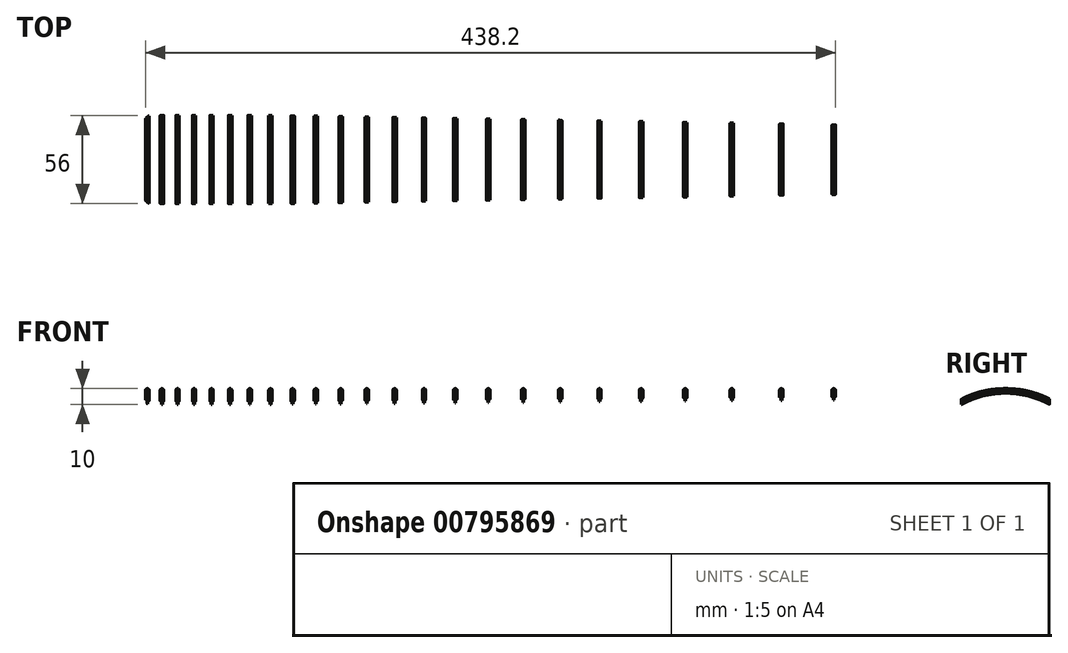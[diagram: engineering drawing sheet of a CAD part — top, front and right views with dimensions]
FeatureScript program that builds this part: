
annotation { "Feature Type Name" : "Feature", "Feature Type Description" : "" }
export const myFeature = defineFeature(function(context is Context, id is Id, definition is map)
    precondition{}
    {
        {
            var Q0;
            Q0=qCreatedBy(makeId("Front.planeOp"),FACE);
            var sketch = newSketch(context, id + "F0", { "sketchPlane" : qUnion([Q0])});
            skLineSegment(sketch, "E0", {"start": v(0.25, 7) * mm, "end": v(471.5, 7) * mm, "construction": true});
            skLineSegment(sketch, "E1", {"start": v(471.5, 7) * mm, "end": v(471.5, 0) * mm, "construction": true});
            skLineSegment(sketch, "E2", {"start": v(436.24, 7) * mm, "end": v(436.24, 0) * mm, "construction": true});
            skLineSegment(sketch, "E3", {"start": v(471.5, 0) * mm, "end": v(0.25, 0) * mm, "construction": true});
            skLineSegment(sketch, "E4", {"start": v(0.25, 0) * mm, "end": v(0.25, 7) * mm, "construction": true});
            skLineSegment(sketch, "E5", {"start": v(402.96, 7) * mm, "end": v(402.96, 0) * mm, "construction": true});
            skLineSegment(sketch, "E6", {"start": v(371.54, 7) * mm, "end": v(371.54, 0) * mm, "construction": true});
            skLineSegment(sketch, "E7", {"start": v(341.88, 7) * mm, "end": v(341.88, 0) * mm, "construction": true});
            skLineSegment(sketch, "E8", {"start": v(313.89, 7) * mm, "end": v(313.89, 0) * mm, "construction": true});
            skLineSegment(sketch, "E9", {"start": v(287.47, 7) * mm, "end": v(287.47, 0) * mm, "construction": true});
            skLineSegment(sketch, "E10", {"start": v(262.53, 7) * mm, "end": v(262.53, 0) * mm, "construction": true});
            skLineSegment(sketch, "E11", {"start": v(239, 7) * mm, "end": v(239, 0) * mm, "construction": true});
            skLineSegment(sketch, "E12", {"start": v(216.79, 7) * mm, "end": v(216.79, 0) * mm, "construction": true});
            skLineSegment(sketch, "E13", {"start": v(195.82, 7) * mm, "end": v(195.82, 0) * mm, "construction": true});
            skLineSegment(sketch, "E14", {"start": v(176.02, 7) * mm, "end": v(176.02, 0) * mm, "construction": true});
            skLineSegment(sketch, "E15", {"start": v(157.34, 7) * mm, "end": v(157.34, 0) * mm, "construction": true});
            skLineSegment(sketch, "E16", {"start": v(139.7, 7) * mm, "end": v(139.7, 0) * mm, "construction": true});
            skLineSegment(sketch, "E17", {"start": v(123.07, 7) * mm, "end": v(123.07, 0) * mm, "construction": true});
            skLineSegment(sketch, "E18", {"start": v(107.36, 7) * mm, "end": v(107.36, 0) * mm, "construction": true});
            skLineSegment(sketch, "E19", {"start": v(92.53, 7) * mm, "end": v(92.53, 0) * mm, "construction": true});
            skLineSegment(sketch, "E20", {"start": v(78.53, 7) * mm, "end": v(78.53, 0) * mm, "construction": true});
            skLineSegment(sketch, "E21", {"start": v(65.32, 7) * mm, "end": v(65.32, 0) * mm, "construction": true});
            skLineSegment(sketch, "E22", {"start": v(52.85, 7) * mm, "end": v(52.85, 0) * mm, "construction": true});
            skLineSegment(sketch, "E23", {"start": v(41.09, 7) * mm, "end": v(41.09, 0) * mm, "construction": true});
            skLineSegment(sketch, "E24", {"start": v(29.98, 7) * mm, "end": v(29.98, 0) * mm, "construction": true});
            skLineSegment(sketch, "E25", {"start": v(19.5, 7) * mm, "end": v(19.5, 0) * mm, "construction": true});
            skLineSegment(sketch, "E26", {"start": v(9.6, 7) * mm, "end": v(9.6, 0) * mm, "construction": true});
            skLineSegment(sketch, "E27", {"start": v(471.76, 7) * mm, "end": v(471.76, 0) * mm});
            skLineSegment(sketch, "E28", {"start": v(471.76, 0) * mm, "end": v(471.26, 0) * mm});
            skLineSegment(sketch, "E29", {"start": v(471.26, 0) * mm, "end": v(471.26, 7) * mm});
            skLineSegment(sketch, "E30", {"start": v(471.26, 7) * mm, "end": v(471.76, 7) * mm});
            skLineSegment(sketch, "E31", {"start": v(436, 7) * mm, "end": v(436.5, 7) * mm});
            skLineSegment(sketch, "E32", {"start": v(436.5, 7) * mm, "end": v(436.5, 0) * mm});
            skLineSegment(sketch, "E33", {"start": v(436.5, 0) * mm, "end": v(436, 0) * mm});
            skLineSegment(sketch, "E34", {"start": v(436, 0) * mm, "end": v(436, 7) * mm});
            skLineSegment(sketch, "E35.bottom", {"start": v(402.7, 7) * mm, "end": v(403.2, 7) * mm});
            skLineSegment(sketch, "E35.top", {"start": v(402.7, 0) * mm, "end": v(403.2, 0) * mm});
            skLineSegment(sketch, "E35.left", {"start": v(402.7, 7) * mm, "end": v(402.7, 0) * mm});
            skLineSegment(sketch, "E35.right", {"start": v(403.2, 7) * mm, "end": v(403.2, 0) * mm});
            skLineSegment(sketch, "E36.bottom", {"start": v(371.29, 7) * mm, "end": v(371.79, 7) * mm});
            skLineSegment(sketch, "E36.top", {"start": v(371.29, 0) * mm, "end": v(371.79, 0) * mm});
            skLineSegment(sketch, "E36.left", {"start": v(371.29, 7) * mm, "end": v(371.29, 0) * mm});
            skLineSegment(sketch, "E36.right", {"start": v(371.79, 7) * mm, "end": v(371.79, 0) * mm});
            skLineSegment(sketch, "E37.bottom", {"start": v(341.63, 7) * mm, "end": v(342.13, 7) * mm});
            skLineSegment(sketch, "E37.top", {"start": v(341.63, 0) * mm, "end": v(342.13, 0) * mm});
            skLineSegment(sketch, "E37.left", {"start": v(341.63, 7) * mm, "end": v(341.63, 0) * mm});
            skLineSegment(sketch, "E37.right", {"start": v(342.13, 7) * mm, "end": v(342.13, 0) * mm});
            skLineSegment(sketch, "E38.bottom", {"start": v(313.64, 7) * mm, "end": v(314.14, 7) * mm});
            skLineSegment(sketch, "E38.top", {"start": v(313.64, 0) * mm, "end": v(314.14, 0) * mm});
            skLineSegment(sketch, "E38.left", {"start": v(313.64, 7) * mm, "end": v(313.64, 0) * mm});
            skLineSegment(sketch, "E38.right", {"start": v(314.14, 7) * mm, "end": v(314.14, 0) * mm});
            skLineSegment(sketch, "E39.bottom", {"start": v(287.22, 7) * mm, "end": v(287.72, 7) * mm});
            skLineSegment(sketch, "E39.top", {"start": v(287.22, 0) * mm, "end": v(287.72, 0) * mm});
            skLineSegment(sketch, "E39.left", {"start": v(287.22, 7) * mm, "end": v(287.22, 0) * mm});
            skLineSegment(sketch, "E39.right", {"start": v(287.72, 7) * mm, "end": v(287.72, 0) * mm});
            skLineSegment(sketch, "E40.bottom", {"start": v(262.28, 7) * mm, "end": v(262.78, 7) * mm});
            skLineSegment(sketch, "E40.top", {"start": v(262.28, 0) * mm, "end": v(262.78, 0) * mm});
            skLineSegment(sketch, "E40.left", {"start": v(262.28, 7) * mm, "end": v(262.28, 0) * mm});
            skLineSegment(sketch, "E40.right", {"start": v(262.78, 7) * mm, "end": v(262.78, 0) * mm});
            skLineSegment(sketch, "E41.bottom", {"start": v(238.75, 7) * mm, "end": v(239.25, 7) * mm});
            skLineSegment(sketch, "E41.top", {"start": v(238.75, 0) * mm, "end": v(239.25, 0) * mm});
            skLineSegment(sketch, "E41.left", {"start": v(238.75, 7) * mm, "end": v(238.75, 0) * mm});
            skLineSegment(sketch, "E41.right", {"start": v(239.25, 7) * mm, "end": v(239.25, 0) * mm});
            skLineSegment(sketch, "E42.bottom", {"start": v(216.54, 7) * mm, "end": v(217.04, 7) * mm});
            skLineSegment(sketch, "E42.top", {"start": v(216.54, 0) * mm, "end": v(217.04, 0) * mm});
            skLineSegment(sketch, "E42.left", {"start": v(216.54, 7) * mm, "end": v(216.54, 0) * mm});
            skLineSegment(sketch, "E42.right", {"start": v(217.04, 7) * mm, "end": v(217.04, 0) * mm});
            skLineSegment(sketch, "E43.bottom", {"start": v(195.57, 7) * mm, "end": v(196.07, 7) * mm});
            skLineSegment(sketch, "E43.top", {"start": v(195.57, 0) * mm, "end": v(196.07, 0) * mm});
            skLineSegment(sketch, "E43.left", {"start": v(195.57, 7) * mm, "end": v(195.57, 0) * mm});
            skLineSegment(sketch, "E43.right", {"start": v(196.07, 7) * mm, "end": v(196.07, 0) * mm});
            skLineSegment(sketch, "E44.bottom", {"start": v(175.77, 7) * mm, "end": v(176.27, 7) * mm});
            skLineSegment(sketch, "E44.top", {"start": v(175.77, 0) * mm, "end": v(176.27, 0) * mm});
            skLineSegment(sketch, "E44.left", {"start": v(175.77, 7) * mm, "end": v(175.77, 0) * mm});
            skLineSegment(sketch, "E44.right", {"start": v(176.27, 7) * mm, "end": v(176.27, 0) * mm});
            skLineSegment(sketch, "E45.bottom", {"start": v(157.1, 7) * mm, "end": v(157.6, 7) * mm});
            skLineSegment(sketch, "E45.top", {"start": v(157.1, 0) * mm, "end": v(157.6, 0) * mm});
            skLineSegment(sketch, "E45.left", {"start": v(157.1, 7) * mm, "end": v(157.1, 0) * mm});
            skLineSegment(sketch, "E45.right", {"start": v(157.6, 7) * mm, "end": v(157.6, 0) * mm});
            skLineSegment(sketch, "E46.bottom", {"start": v(139.46, 7) * mm, "end": v(139.96, 7) * mm});
            skLineSegment(sketch, "E46.top", {"start": v(139.46, 0) * mm, "end": v(139.96, 0) * mm});
            skLineSegment(sketch, "E46.left", {"start": v(139.46, 7) * mm, "end": v(139.46, 0) * mm});
            skLineSegment(sketch, "E46.right", {"start": v(139.96, 7) * mm, "end": v(139.96, 0) * mm});
            skLineSegment(sketch, "E47.bottom", {"start": v(122.82, 7) * mm, "end": v(123.32, 7) * mm});
            skLineSegment(sketch, "E47.top", {"start": v(122.82, 0) * mm, "end": v(123.32, 0) * mm});
            skLineSegment(sketch, "E47.left", {"start": v(122.82, 7) * mm, "end": v(122.82, 0) * mm});
            skLineSegment(sketch, "E47.right", {"start": v(123.32, 7) * mm, "end": v(123.32, 0) * mm});
            skLineSegment(sketch, "E48.bottom", {"start": v(107.1, 7) * mm, "end": v(107.6, 7) * mm});
            skLineSegment(sketch, "E48.top", {"start": v(107.1, 0) * mm, "end": v(107.6, 0) * mm});
            skLineSegment(sketch, "E48.left", {"start": v(107.1, 7) * mm, "end": v(107.1, 0) * mm});
            skLineSegment(sketch, "E48.right", {"start": v(107.6, 7) * mm, "end": v(107.6, 0) * mm});
            skLineSegment(sketch, "E49.bottom", {"start": v(92.28, 7) * mm, "end": v(92.78, 7) * mm});
            skLineSegment(sketch, "E49.top", {"start": v(92.28, 0) * mm, "end": v(92.78, 0) * mm});
            skLineSegment(sketch, "E49.left", {"start": v(92.28, 7) * mm, "end": v(92.28, 0) * mm});
            skLineSegment(sketch, "E49.right", {"start": v(92.78, 7) * mm, "end": v(92.78, 0) * mm});
            skLineSegment(sketch, "E50.bottom", {"start": v(78.28, 7) * mm, "end": v(78.78, 7) * mm});
            skLineSegment(sketch, "E50.top", {"start": v(78.28, 0) * mm, "end": v(78.78, 0) * mm});
            skLineSegment(sketch, "E50.left", {"start": v(78.28, 7) * mm, "end": v(78.28, 0) * mm});
            skLineSegment(sketch, "E50.right", {"start": v(78.78, 7) * mm, "end": v(78.78, 0) * mm});
            skLineSegment(sketch, "E51.bottom", {"start": v(65.07, 7) * mm, "end": v(65.57, 7) * mm});
            skLineSegment(sketch, "E51.top", {"start": v(65.07, 0) * mm, "end": v(65.57, 0) * mm});
            skLineSegment(sketch, "E51.left", {"start": v(65.07, 7) * mm, "end": v(65.07, 0) * mm});
            skLineSegment(sketch, "E51.right", {"start": v(65.57, 7) * mm, "end": v(65.57, 0) * mm});
            skLineSegment(sketch, "E52.bottom", {"start": v(52.6, 7) * mm, "end": v(53.1, 7) * mm});
            skLineSegment(sketch, "E52.top", {"start": v(52.6, 0) * mm, "end": v(53.1, 0) * mm});
            skLineSegment(sketch, "E52.left", {"start": v(52.6, 7) * mm, "end": v(52.6, 0) * mm});
            skLineSegment(sketch, "E52.right", {"start": v(53.1, 7) * mm, "end": v(53.1, 0) * mm});
            skLineSegment(sketch, "E53.bottom", {"start": v(40.84, 7) * mm, "end": v(41.34, 7) * mm});
            skLineSegment(sketch, "E53.top", {"start": v(40.84, 0) * mm, "end": v(41.34, 0) * mm});
            skLineSegment(sketch, "E53.left", {"start": v(40.84, 7) * mm, "end": v(40.84, 0) * mm});
            skLineSegment(sketch, "E53.right", {"start": v(41.34, 7) * mm, "end": v(41.34, 0) * mm});
            skLineSegment(sketch, "E54.bottom", {"start": v(0, 7) * mm, "end": v(0.5, 7) * mm});
            skLineSegment(sketch, "E54.top", {"start": v(0, 0) * mm, "end": v(0.5, 0) * mm});
            skLineSegment(sketch, "E54.left", {"start": v(0, 7) * mm, "end": v(0, 0) * mm});
            skLineSegment(sketch, "E54.right", {"start": v(0.5, 7) * mm, "end": v(0.5, 0) * mm});
            skLineSegment(sketch, "E55.bottom", {"start": v(9.35, 7) * mm, "end": v(9.85, 7) * mm});
            skLineSegment(sketch, "E55.top", {"start": v(9.35, 0) * mm, "end": v(9.85, 0) * mm});
            skLineSegment(sketch, "E55.left", {"start": v(9.35, 7) * mm, "end": v(9.35, 0) * mm});
            skLineSegment(sketch, "E55.right", {"start": v(9.85, 7) * mm, "end": v(9.85, 0) * mm});
            skLineSegment(sketch, "E56.bottom", {"start": v(19.24, 0) * mm, "end": v(19.74, 0) * mm});
            skLineSegment(sketch, "E56.top", {"start": v(19.24, 7) * mm, "end": v(19.74, 7) * mm});
            skLineSegment(sketch, "E56.left", {"start": v(19.24, 0) * mm, "end": v(19.24, 7) * mm});
            skLineSegment(sketch, "E56.right", {"start": v(19.74, 0) * mm, "end": v(19.74, 7) * mm});
            skLineSegment(sketch, "E57.bottom", {"start": v(29.73, 7) * mm, "end": v(30.23, 7) * mm});
            skLineSegment(sketch, "E57.top", {"start": v(29.73, 0) * mm, "end": v(30.23, 0) * mm});
            skLineSegment(sketch, "E57.left", {"start": v(29.73, 7) * mm, "end": v(29.73, 0) * mm});
            skLineSegment(sketch, "E57.right", {"start": v(30.23, 7) * mm, "end": v(30.23, 0) * mm});
            skSolve(sketch);
        }
        {
            var Q0;
            Q0=qCreatedBy(makeId("Front.planeOp"),FACE);
            var sketch = newSketch(context, id + "F1", { "sketchPlane" : qUnion([Q0])});
            skLineSegment(sketch, "E58", {"start": v(436, 5.27) * mm, "end": v(436.5, 5.27) * mm});
            skLineSegment(sketch, "E59", {"start": v(436.5, 5.27) * mm, "end": v(436.5, 6.85) * mm});
            skLineSegment(sketch, "E60", {"start": v(436, 5.27) * mm, "end": v(436, 6.85) * mm});
            skArc(sketch, "E61", {"start": v(435.15, 7.32) * mm, "mid": v(436.24, 8.14) * mm, "end": v(437.34, 7.32) * mm});
            skLineSegment(sketch, "E62", {"start": v(435.39, 7) * mm, "end": v(435.84, 7) * mm});
            skLineSegment(sketch, "E63", {"start": v(437.1, 7) * mm, "end": v(436.64, 7) * mm});
            skPoint(sketch, "E64.visualSharp", {"position": v(437.38, 7) * mm});
            skArc(sketch, "E64.filletArc", {"start": v(437.1, 7) * mm, "mid": v(437.3, 7.1) * mm, "end": v(437.34, 7.32) * mm});
            skPoint(sketch, "E65.visualSharp", {"position": v(435.1, 7) * mm});
            skArc(sketch, "E65.filletArc", {"start": v(435.15, 7.32) * mm, "mid": v(435.19, 7.1) * mm, "end": v(435.39, 7) * mm});
            skPoint(sketch, "E66.visualSharp", {"position": v(436.5, 7) * mm});
            skArc(sketch, "E66.filletArc", {"start": v(436.64, 7) * mm, "mid": v(436.54, 6.96) * mm, "end": v(436.5, 6.85) * mm});
            skPoint(sketch, "E67.visualSharp", {"position": v(436, 7) * mm});
            skArc(sketch, "E67.filletArc", {"start": v(436, 6.85) * mm, "mid": v(435.95, 6.96) * mm, "end": v(435.84, 7) * mm});
            skPoint(sketch, "E68.endSnap0", {"position": v(436.24, 8.14) * mm});
            skLineSegment(sketch, "E69", {"start": v(436.24, 8.14) * mm, "end": v(436.24, -53.3) * mm, "construction": true});
            skLineSegment(sketch, "E70", {"start": v(402.7, 5.27) * mm, "end": v(403.2, 5.27) * mm});
            skLineSegment(sketch, "E71", {"start": v(403.2, 5.27) * mm, "end": v(403.2, 6.85) * mm});
            skLineSegment(sketch, "E72", {"start": v(402.7, 5.27) * mm, "end": v(402.7, 6.85) * mm});
            skArc(sketch, "E73", {"start": v(401.86, 7.32) * mm, "mid": v(402.96, 8.14) * mm, "end": v(404.05, 7.32) * mm});
            skLineSegment(sketch, "E74", {"start": v(402.1, 7) * mm, "end": v(402.56, 7) * mm});
            skLineSegment(sketch, "E75", {"start": v(403.8, 7) * mm, "end": v(403.36, 7) * mm});
            skPoint(sketch, "E76.visualSharp", {"position": v(404.1, 7) * mm});
            skArc(sketch, "E76.filletArc", {"start": v(403.8, 7) * mm, "mid": v(404, 7.1) * mm, "end": v(404.05, 7.32) * mm});
            skPoint(sketch, "E77.visualSharp", {"position": v(401.82, 7) * mm});
            skArc(sketch, "E77.filletArc", {"start": v(401.86, 7.32) * mm, "mid": v(401.9, 7.1) * mm, "end": v(402.1, 7) * mm});
            skPoint(sketch, "E78.visualSharp", {"position": v(403.2, 7) * mm});
            skArc(sketch, "E78.filletArc", {"start": v(403.36, 7) * mm, "mid": v(403.25, 6.96) * mm, "end": v(403.2, 6.85) * mm});
            skPoint(sketch, "E79.visualSharp", {"position": v(402.7, 7) * mm});
            skArc(sketch, "E79.filletArc", {"start": v(402.7, 6.85) * mm, "mid": v(402.66, 6.96) * mm, "end": v(402.56, 7) * mm});
            skPoint(sketch, "E80.endSnap0", {"position": v(402.96, 8.14) * mm});
            skLineSegment(sketch, "E81", {"start": v(402.96, 8.14) * mm, "end": v(402.96, -53.3) * mm, "construction": true});
            skLineSegment(sketch, "E82", {"start": v(371.29, 5.27) * mm, "end": v(371.79, 5.27) * mm});
            skLineSegment(sketch, "E83", {"start": v(371.79, 5.27) * mm, "end": v(371.79, 6.85) * mm});
            skLineSegment(sketch, "E84", {"start": v(371.29, 5.27) * mm, "end": v(371.29, 6.85) * mm});
            skArc(sketch, "E85", {"start": v(370.44, 7.32) * mm, "mid": v(371.54, 8.14) * mm, "end": v(372.63, 7.32) * mm});
            skLineSegment(sketch, "E86", {"start": v(370.68, 7) * mm, "end": v(371.14, 7) * mm});
            skLineSegment(sketch, "E87", {"start": v(372.4, 7) * mm, "end": v(371.94, 7) * mm});
            skPoint(sketch, "E88.visualSharp", {"position": v(372.68, 7) * mm});
            skArc(sketch, "E88.filletArc", {"start": v(372.4, 7) * mm, "mid": v(372.6, 7.1) * mm, "end": v(372.63, 7.32) * mm});
            skPoint(sketch, "E89.visualSharp", {"position": v(370.4, 7) * mm});
            skArc(sketch, "E89.filletArc", {"start": v(370.44, 7.32) * mm, "mid": v(370.48, 7.1) * mm, "end": v(370.68, 7) * mm});
            skPoint(sketch, "E90.visualSharp", {"position": v(371.79, 7) * mm});
            skArc(sketch, "E90.filletArc", {"start": v(371.94, 7) * mm, "mid": v(371.83, 6.96) * mm, "end": v(371.79, 6.85) * mm});
            skPoint(sketch, "E91.visualSharp", {"position": v(371.29, 7) * mm});
            skArc(sketch, "E91.filletArc", {"start": v(371.29, 6.85) * mm, "mid": v(371.24, 6.96) * mm, "end": v(371.14, 7) * mm});
            skPoint(sketch, "E92.endSnap0", {"position": v(371.54, 8.14) * mm});
            skLineSegment(sketch, "E93", {"start": v(371.54, 8.14) * mm, "end": v(371.54, -53.3) * mm, "construction": true});
            skLineSegment(sketch, "E94", {"start": v(341.63, 5.27) * mm, "end": v(342.13, 5.27) * mm});
            skLineSegment(sketch, "E95", {"start": v(342.13, 5.27) * mm, "end": v(342.13, 6.85) * mm});
            skLineSegment(sketch, "E96", {"start": v(341.63, 5.27) * mm, "end": v(341.63, 6.85) * mm});
            skArc(sketch, "E97", {"start": v(340.79, 7.32) * mm, "mid": v(341.88, 8.14) * mm, "end": v(342.97, 7.32) * mm});
            skLineSegment(sketch, "E98", {"start": v(341.03, 7) * mm, "end": v(341.48, 7) * mm});
            skLineSegment(sketch, "E99", {"start": v(342.73, 7) * mm, "end": v(342.28, 7) * mm});
            skPoint(sketch, "E100.visualSharp", {"position": v(343.02, 7) * mm});
            skArc(sketch, "E100.filletArc", {"start": v(342.73, 7) * mm, "mid": v(342.93, 7.1) * mm, "end": v(342.97, 7.32) * mm});
            skPoint(sketch, "E101.visualSharp", {"position": v(340.74, 7) * mm});
            skArc(sketch, "E101.filletArc", {"start": v(340.79, 7.32) * mm, "mid": v(340.83, 7.1) * mm, "end": v(341.03, 7) * mm});
            skPoint(sketch, "E102.visualSharp", {"position": v(342.13, 7) * mm});
            skArc(sketch, "E102.filletArc", {"start": v(342.28, 7) * mm, "mid": v(342.17, 6.96) * mm, "end": v(342.13, 6.85) * mm});
            skPoint(sketch, "E103.visualSharp", {"position": v(341.63, 7) * mm});
            skArc(sketch, "E103.filletArc", {"start": v(341.63, 6.85) * mm, "mid": v(341.59, 6.96) * mm, "end": v(341.48, 7) * mm});
            skPoint(sketch, "E104.endSnap0", {"position": v(341.88, 8.14) * mm});
            skLineSegment(sketch, "E105", {"start": v(341.88, 8.14) * mm, "end": v(341.88, -53.3) * mm, "construction": true});
            skLineSegment(sketch, "E106", {"start": v(313.64, 5.27) * mm, "end": v(314.14, 5.27) * mm});
            skLineSegment(sketch, "E107", {"start": v(314.14, 5.27) * mm, "end": v(314.14, 6.85) * mm});
            skLineSegment(sketch, "E108", {"start": v(313.64, 5.27) * mm, "end": v(313.64, 6.85) * mm});
            skArc(sketch, "E109", {"start": v(312.8, 7.32) * mm, "mid": v(313.89, 8.14) * mm, "end": v(314.98, 7.32) * mm});
            skLineSegment(sketch, "E110", {"start": v(313.03, 7) * mm, "end": v(313.49, 7) * mm});
            skLineSegment(sketch, "E111", {"start": v(314.74, 7) * mm, "end": v(314.29, 7) * mm});
            skPoint(sketch, "E112.visualSharp", {"position": v(315.03, 7) * mm});
            skArc(sketch, "E112.filletArc", {"start": v(314.74, 7) * mm, "mid": v(314.94, 7.1) * mm, "end": v(314.98, 7.32) * mm});
            skPoint(sketch, "E113.visualSharp", {"position": v(312.75, 7) * mm});
            skArc(sketch, "E113.filletArc", {"start": v(312.8, 7.32) * mm, "mid": v(312.83, 7.1) * mm, "end": v(313.03, 7) * mm});
            skPoint(sketch, "E114.visualSharp", {"position": v(314.14, 7) * mm});
            skArc(sketch, "E114.filletArc", {"start": v(314.29, 7) * mm, "mid": v(314.18, 6.96) * mm, "end": v(314.14, 6.85) * mm});
            skPoint(sketch, "E115.visualSharp", {"position": v(313.64, 7) * mm});
            skArc(sketch, "E115.filletArc", {"start": v(313.64, 6.85) * mm, "mid": v(313.6, 6.96) * mm, "end": v(313.49, 7) * mm});
            skPoint(sketch, "E116.endSnap0", {"position": v(313.89, 8.14) * mm});
            skLineSegment(sketch, "E117", {"start": v(313.89, 8.14) * mm, "end": v(313.89, -53.3) * mm, "construction": true});
            skLineSegment(sketch, "E118", {"start": v(287.22, 5.27) * mm, "end": v(287.72, 5.27) * mm});
            skLineSegment(sketch, "E119", {"start": v(287.72, 5.27) * mm, "end": v(287.72, 6.85) * mm});
            skLineSegment(sketch, "E120", {"start": v(287.22, 5.27) * mm, "end": v(287.22, 6.85) * mm});
            skArc(sketch, "E121", {"start": v(286.37, 7.32) * mm, "mid": v(287.47, 8.14) * mm, "end": v(288.56, 7.32) * mm});
            skLineSegment(sketch, "E122", {"start": v(286.61, 7) * mm, "end": v(287.07, 7) * mm});
            skLineSegment(sketch, "E123", {"start": v(288.32, 7) * mm, "end": v(287.87, 7) * mm});
            skPoint(sketch, "E124.visualSharp", {"position": v(288.6, 7) * mm});
            skArc(sketch, "E124.filletArc", {"start": v(288.32, 7) * mm, "mid": v(288.52, 7.1) * mm, "end": v(288.56, 7.32) * mm});
            skPoint(sketch, "E125.visualSharp", {"position": v(286.33, 7) * mm});
            skArc(sketch, "E125.filletArc", {"start": v(286.37, 7.32) * mm, "mid": v(286.41, 7.1) * mm, "end": v(286.61, 7) * mm});
            skPoint(sketch, "E126.visualSharp", {"position": v(287.72, 7) * mm});
            skArc(sketch, "E126.filletArc", {"start": v(287.87, 7) * mm, "mid": v(287.76, 6.96) * mm, "end": v(287.72, 6.85) * mm});
            skPoint(sketch, "E127.visualSharp", {"position": v(287.22, 7) * mm});
            skArc(sketch, "E127.filletArc", {"start": v(287.22, 6.85) * mm, "mid": v(287.17, 6.96) * mm, "end": v(287.07, 7) * mm});
            skPoint(sketch, "E128.endSnap0", {"position": v(287.47, 8.14) * mm});
            skLineSegment(sketch, "E129", {"start": v(287.47, 8.14) * mm, "end": v(287.47, -53.3) * mm, "construction": true});
            skLineSegment(sketch, "E130", {"start": v(262.28, 5.27) * mm, "end": v(262.78, 5.27) * mm});
            skLineSegment(sketch, "E131", {"start": v(262.78, 5.27) * mm, "end": v(262.78, 6.85) * mm});
            skLineSegment(sketch, "E132", {"start": v(262.28, 5.27) * mm, "end": v(262.28, 6.85) * mm});
            skArc(sketch, "E133", {"start": v(261.44, 7.32) * mm, "mid": v(262.53, 8.14) * mm, "end": v(263.63, 7.32) * mm});
            skLineSegment(sketch, "E134", {"start": v(261.68, 7) * mm, "end": v(262.13, 7) * mm});
            skLineSegment(sketch, "E135", {"start": v(263.39, 7) * mm, "end": v(262.93, 7) * mm});
            skPoint(sketch, "E136.visualSharp", {"position": v(263.67, 7) * mm});
            skArc(sketch, "E136.filletArc", {"start": v(263.39, 7) * mm, "mid": v(263.59, 7.1) * mm, "end": v(263.63, 7.32) * mm});
            skPoint(sketch, "E137.visualSharp", {"position": v(261.4, 7) * mm});
            skArc(sketch, "E137.filletArc", {"start": v(261.44, 7.32) * mm, "mid": v(261.48, 7.1) * mm, "end": v(261.68, 7) * mm});
            skPoint(sketch, "E138.visualSharp", {"position": v(262.78, 7) * mm});
            skArc(sketch, "E138.filletArc", {"start": v(262.93, 7) * mm, "mid": v(262.83, 6.96) * mm, "end": v(262.78, 6.85) * mm});
            skPoint(sketch, "E139.visualSharp", {"position": v(262.28, 7) * mm});
            skArc(sketch, "E139.filletArc", {"start": v(262.28, 6.85) * mm, "mid": v(262.24, 6.96) * mm, "end": v(262.13, 7) * mm});
            skPoint(sketch, "E140.endSnap0", {"position": v(262.53, 8.14) * mm});
            skLineSegment(sketch, "E141", {"start": v(262.53, 8.14) * mm, "end": v(262.53, -53.3) * mm, "construction": true});
            skLineSegment(sketch, "E142", {"start": v(238.75, 5.27) * mm, "end": v(239.25, 5.27) * mm});
            skLineSegment(sketch, "E143", {"start": v(239.25, 5.27) * mm, "end": v(239.25, 6.85) * mm});
            skLineSegment(sketch, "E144", {"start": v(238.75, 5.27) * mm, "end": v(238.75, 6.85) * mm});
            skArc(sketch, "E145", {"start": v(237.9, 7.32) * mm, "mid": v(239, 8.14) * mm, "end": v(240.1, 7.32) * mm});
            skLineSegment(sketch, "E146", {"start": v(238.15, 7) * mm, "end": v(238.6, 7) * mm});
            skLineSegment(sketch, "E147", {"start": v(239.86, 7) * mm, "end": v(239.4, 7) * mm});
            skPoint(sketch, "E148.visualSharp", {"position": v(240.14, 7) * mm});
            skArc(sketch, "E148.filletArc", {"start": v(239.86, 7) * mm, "mid": v(240.06, 7.1) * mm, "end": v(240.1, 7.32) * mm});
            skPoint(sketch, "E149.visualSharp", {"position": v(237.86, 7) * mm});
            skArc(sketch, "E149.filletArc", {"start": v(237.9, 7.32) * mm, "mid": v(237.95, 7.1) * mm, "end": v(238.15, 7) * mm});
            skPoint(sketch, "E150.visualSharp", {"position": v(239.25, 7) * mm});
            skArc(sketch, "E150.filletArc", {"start": v(239.4, 7) * mm, "mid": v(239.3, 6.96) * mm, "end": v(239.25, 6.85) * mm});
            skPoint(sketch, "E151.visualSharp", {"position": v(238.75, 7) * mm});
            skArc(sketch, "E151.filletArc", {"start": v(238.75, 6.85) * mm, "mid": v(238.7, 6.96) * mm, "end": v(238.6, 7) * mm});
            skPoint(sketch, "E152.endSnap0", {"position": v(239, 8.14) * mm});
            skLineSegment(sketch, "E153", {"start": v(239, 8.14) * mm, "end": v(239, -53.3) * mm, "construction": true});
            skLineSegment(sketch, "E154", {"start": v(216.54, 5.27) * mm, "end": v(217.04, 5.27) * mm});
            skLineSegment(sketch, "E155", {"start": v(217.04, 5.27) * mm, "end": v(217.04, 6.85) * mm});
            skLineSegment(sketch, "E156", {"start": v(216.54, 5.27) * mm, "end": v(216.54, 6.85) * mm});
            skArc(sketch, "E157", {"start": v(215.7, 7.32) * mm, "mid": v(216.79, 8.14) * mm, "end": v(217.88, 7.32) * mm});
            skLineSegment(sketch, "E158", {"start": v(215.93, 7) * mm, "end": v(216.39, 7) * mm});
            skLineSegment(sketch, "E159", {"start": v(217.64, 7) * mm, "end": v(217.19, 7) * mm});
            skPoint(sketch, "E160.visualSharp", {"position": v(217.93, 7) * mm});
            skArc(sketch, "E160.filletArc", {"start": v(217.64, 7) * mm, "mid": v(217.84, 7.1) * mm, "end": v(217.88, 7.32) * mm});
            skPoint(sketch, "E161.visualSharp", {"position": v(215.65, 7) * mm});
            skArc(sketch, "E161.filletArc", {"start": v(215.7, 7.32) * mm, "mid": v(215.73, 7.1) * mm, "end": v(215.93, 7) * mm});
            skPoint(sketch, "E162.visualSharp", {"position": v(217.04, 7) * mm});
            skArc(sketch, "E162.filletArc", {"start": v(217.19, 7) * mm, "mid": v(217.08, 6.96) * mm, "end": v(217.04, 6.85) * mm});
            skPoint(sketch, "E163.visualSharp", {"position": v(216.54, 7) * mm});
            skArc(sketch, "E163.filletArc", {"start": v(216.54, 6.85) * mm, "mid": v(216.5, 6.96) * mm, "end": v(216.39, 7) * mm});
            skPoint(sketch, "E164.endSnap0", {"position": v(216.79, 8.14) * mm});
            skLineSegment(sketch, "E165", {"start": v(216.79, 8.14) * mm, "end": v(216.79, -53.3) * mm, "construction": true});
            skLineSegment(sketch, "E166", {"start": v(195.57, 5.27) * mm, "end": v(196.07, 5.27) * mm});
            skLineSegment(sketch, "E167", {"start": v(196.07, 5.27) * mm, "end": v(196.07, 6.85) * mm});
            skLineSegment(sketch, "E168", {"start": v(195.57, 5.27) * mm, "end": v(195.57, 6.85) * mm});
            skArc(sketch, "E169", {"start": v(194.72, 7.32) * mm, "mid": v(195.82, 8.14) * mm, "end": v(196.91, 7.32) * mm});
            skLineSegment(sketch, "E170", {"start": v(194.96, 7) * mm, "end": v(195.42, 7) * mm});
            skLineSegment(sketch, "E171", {"start": v(196.67, 7) * mm, "end": v(196.22, 7) * mm});
            skPoint(sketch, "E172.visualSharp", {"position": v(196.96, 7) * mm});
            skArc(sketch, "E172.filletArc", {"start": v(196.67, 7) * mm, "mid": v(196.87, 7.1) * mm, "end": v(196.91, 7.32) * mm});
            skPoint(sketch, "E173.visualSharp", {"position": v(194.68, 7) * mm});
            skArc(sketch, "E173.filletArc", {"start": v(194.72, 7.32) * mm, "mid": v(194.76, 7.1) * mm, "end": v(194.96, 7) * mm});
            skPoint(sketch, "E174.visualSharp", {"position": v(196.07, 7) * mm});
            skArc(sketch, "E174.filletArc", {"start": v(196.22, 7) * mm, "mid": v(196.11, 6.96) * mm, "end": v(196.07, 6.85) * mm});
            skPoint(sketch, "E175.visualSharp", {"position": v(195.57, 7) * mm});
            skArc(sketch, "E175.filletArc", {"start": v(195.57, 6.85) * mm, "mid": v(195.52, 6.96) * mm, "end": v(195.42, 7) * mm});
            skPoint(sketch, "E176.endSnap0", {"position": v(195.82, 8.14) * mm});
            skLineSegment(sketch, "E177", {"start": v(195.82, 8.14) * mm, "end": v(195.82, -53.3) * mm, "construction": true});
            skLineSegment(sketch, "E178", {"start": v(175.77, 5.27) * mm, "end": v(176.27, 5.27) * mm});
            skLineSegment(sketch, "E179", {"start": v(176.27, 5.27) * mm, "end": v(176.27, 6.85) * mm});
            skLineSegment(sketch, "E180", {"start": v(175.77, 5.27) * mm, "end": v(175.77, 6.85) * mm});
            skArc(sketch, "E181", {"start": v(174.93, 7.32) * mm, "mid": v(176.02, 8.14) * mm, "end": v(177.12, 7.32) * mm});
            skLineSegment(sketch, "E182", {"start": v(175.17, 7) * mm, "end": v(175.62, 7) * mm});
            skLineSegment(sketch, "E183", {"start": v(176.88, 7) * mm, "end": v(176.42, 7) * mm});
            skPoint(sketch, "E184.visualSharp", {"position": v(177.16, 7) * mm});
            skArc(sketch, "E184.filletArc", {"start": v(176.88, 7) * mm, "mid": v(177.08, 7.1) * mm, "end": v(177.12, 7.32) * mm});
            skPoint(sketch, "E185.visualSharp", {"position": v(174.88, 7) * mm});
            skArc(sketch, "E185.filletArc", {"start": v(174.93, 7.32) * mm, "mid": v(174.97, 7.1) * mm, "end": v(175.17, 7) * mm});
            skPoint(sketch, "E186.visualSharp", {"position": v(176.27, 7) * mm});
            skArc(sketch, "E186.filletArc", {"start": v(176.42, 7) * mm, "mid": v(176.32, 6.96) * mm, "end": v(176.27, 6.85) * mm});
            skPoint(sketch, "E187.visualSharp", {"position": v(175.77, 7) * mm});
            skArc(sketch, "E187.filletArc", {"start": v(175.77, 6.85) * mm, "mid": v(175.73, 6.96) * mm, "end": v(175.62, 7) * mm});
            skPoint(sketch, "E188.endSnap0", {"position": v(176.02, 8.14) * mm});
            skLineSegment(sketch, "E189", {"start": v(176.02, 8.14) * mm, "end": v(176.02, -53.3) * mm, "construction": true});
            skLineSegment(sketch, "E190", {"start": v(157.1, 5.27) * mm, "end": v(157.6, 5.27) * mm});
            skLineSegment(sketch, "E191", {"start": v(157.6, 5.27) * mm, "end": v(157.6, 6.85) * mm});
            skLineSegment(sketch, "E192", {"start": v(157.1, 5.27) * mm, "end": v(157.1, 6.85) * mm});
            skArc(sketch, "E193", {"start": v(156.25, 7.32) * mm, "mid": v(157.34, 8.14) * mm, "end": v(158.44, 7.32) * mm});
            skLineSegment(sketch, "E194", {"start": v(156.49, 7) * mm, "end": v(156.94, 7) * mm});
            skLineSegment(sketch, "E195", {"start": v(158.2, 7) * mm, "end": v(157.74, 7) * mm});
            skPoint(sketch, "E196.visualSharp", {"position": v(158.48, 7) * mm});
            skArc(sketch, "E196.filletArc", {"start": v(158.2, 7) * mm, "mid": v(158.4, 7.1) * mm, "end": v(158.44, 7.32) * mm});
            skPoint(sketch, "E197.visualSharp", {"position": v(156.2, 7) * mm});
            skArc(sketch, "E197.filletArc", {"start": v(156.25, 7.32) * mm, "mid": v(156.29, 7.1) * mm, "end": v(156.49, 7) * mm});
            skPoint(sketch, "E198.visualSharp", {"position": v(157.6, 7) * mm});
            skArc(sketch, "E198.filletArc", {"start": v(157.74, 7) * mm, "mid": v(157.64, 6.96) * mm, "end": v(157.6, 6.85) * mm});
            skPoint(sketch, "E199.visualSharp", {"position": v(157.1, 7) * mm});
            skArc(sketch, "E199.filletArc", {"start": v(157.1, 6.85) * mm, "mid": v(157.05, 6.96) * mm, "end": v(156.94, 7) * mm});
            skPoint(sketch, "E200.endSnap0", {"position": v(157.34, 8.14) * mm});
            skLineSegment(sketch, "E201", {"start": v(157.34, 8.14) * mm, "end": v(157.34, -53.3) * mm, "construction": true});
            skLineSegment(sketch, "E202", {"start": v(139.46, 5.27) * mm, "end": v(139.96, 5.27) * mm});
            skLineSegment(sketch, "E203", {"start": v(139.96, 5.27) * mm, "end": v(139.96, 6.85) * mm});
            skLineSegment(sketch, "E204", {"start": v(139.46, 5.27) * mm, "end": v(139.46, 6.85) * mm});
            skArc(sketch, "E205", {"start": v(138.62, 7.32) * mm, "mid": v(139.7, 8.14) * mm, "end": v(140.8, 7.32) * mm});
            skLineSegment(sketch, "E206", {"start": v(138.86, 7) * mm, "end": v(139.3, 7) * mm});
            skLineSegment(sketch, "E207", {"start": v(140.56, 7) * mm, "end": v(140.1, 7) * mm});
            skPoint(sketch, "E208.visualSharp", {"position": v(140.85, 7) * mm});
            skArc(sketch, "E208.filletArc", {"start": v(140.56, 7) * mm, "mid": v(140.76, 7.1) * mm, "end": v(140.8, 7.32) * mm});
            skPoint(sketch, "E209.visualSharp", {"position": v(138.57, 7) * mm});
            skArc(sketch, "E209.filletArc", {"start": v(138.62, 7.32) * mm, "mid": v(138.66, 7.1) * mm, "end": v(138.86, 7) * mm});
            skPoint(sketch, "E210.visualSharp", {"position": v(139.96, 7) * mm});
            skArc(sketch, "E210.filletArc", {"start": v(140.1, 7) * mm, "mid": v(140, 6.96) * mm, "end": v(139.96, 6.85) * mm});
            skPoint(sketch, "E211.visualSharp", {"position": v(139.46, 7) * mm});
            skArc(sketch, "E211.filletArc", {"start": v(139.46, 6.85) * mm, "mid": v(139.42, 6.96) * mm, "end": v(139.3, 7) * mm});
            skPoint(sketch, "E212.endSnap0", {"position": v(139.7, 8.14) * mm});
            skLineSegment(sketch, "E213", {"start": v(139.7, 8.14) * mm, "end": v(139.7, -53.3) * mm, "construction": true});
            skLineSegment(sketch, "E214", {"start": v(122.82, 5.27) * mm, "end": v(123.32, 5.27) * mm});
            skLineSegment(sketch, "E215", {"start": v(123.32, 5.27) * mm, "end": v(123.32, 6.85) * mm});
            skLineSegment(sketch, "E216", {"start": v(122.82, 5.27) * mm, "end": v(122.82, 6.85) * mm});
            skArc(sketch, "E217", {"start": v(121.97, 7.32) * mm, "mid": v(123.07, 8.14) * mm, "end": v(124.16, 7.32) * mm});
            skLineSegment(sketch, "E218", {"start": v(122.21, 7) * mm, "end": v(122.67, 7) * mm});
            skLineSegment(sketch, "E219", {"start": v(123.92, 7) * mm, "end": v(123.47, 7) * mm});
            skPoint(sketch, "E220.visualSharp", {"position": v(124.2, 7) * mm});
            skArc(sketch, "E220.filletArc", {"start": v(123.92, 7) * mm, "mid": v(124.12, 7.1) * mm, "end": v(124.16, 7.32) * mm});
            skPoint(sketch, "E221.visualSharp", {"position": v(121.93, 7) * mm});
            skArc(sketch, "E221.filletArc", {"start": v(121.97, 7.32) * mm, "mid": v(122.01, 7.1) * mm, "end": v(122.21, 7) * mm});
            skPoint(sketch, "E222.visualSharp", {"position": v(123.32, 7) * mm});
            skArc(sketch, "E222.filletArc", {"start": v(123.47, 7) * mm, "mid": v(123.36, 6.96) * mm, "end": v(123.32, 6.85) * mm});
            skPoint(sketch, "E223.visualSharp", {"position": v(122.82, 7) * mm});
            skArc(sketch, "E223.filletArc", {"start": v(122.82, 6.85) * mm, "mid": v(122.77, 6.96) * mm, "end": v(122.67, 7) * mm});
            skPoint(sketch, "E224.endSnap0", {"position": v(123.07, 8.14) * mm});
            skLineSegment(sketch, "E225", {"start": v(123.07, 8.14) * mm, "end": v(123.07, -53.3) * mm, "construction": true});
            skLineSegment(sketch, "E226", {"start": v(107.1, 5.27) * mm, "end": v(107.6, 5.27) * mm});
            skLineSegment(sketch, "E227", {"start": v(107.6, 5.27) * mm, "end": v(107.6, 6.85) * mm});
            skLineSegment(sketch, "E228", {"start": v(107.1, 5.27) * mm, "end": v(107.1, 6.85) * mm});
            skArc(sketch, "E229", {"start": v(106.26, 7.32) * mm, "mid": v(107.36, 8.14) * mm, "end": v(108.45, 7.32) * mm});
            skLineSegment(sketch, "E230", {"start": v(106.5, 7) * mm, "end": v(106.96, 7) * mm});
            skLineSegment(sketch, "E231", {"start": v(108.21, 7) * mm, "end": v(107.76, 7) * mm});
            skPoint(sketch, "E232.visualSharp", {"position": v(108.5, 7) * mm});
            skArc(sketch, "E232.filletArc", {"start": v(108.21, 7) * mm, "mid": v(108.41, 7.1) * mm, "end": v(108.45, 7.32) * mm});
            skPoint(sketch, "E233.visualSharp", {"position": v(106.22, 7) * mm});
            skArc(sketch, "E233.filletArc", {"start": v(106.26, 7.32) * mm, "mid": v(106.3, 7.1) * mm, "end": v(106.5, 7) * mm});
            skPoint(sketch, "E234.visualSharp", {"position": v(107.6, 7) * mm});
            skArc(sketch, "E234.filletArc", {"start": v(107.76, 7) * mm, "mid": v(107.65, 6.96) * mm, "end": v(107.6, 6.85) * mm});
            skPoint(sketch, "E235.visualSharp", {"position": v(107.1, 7) * mm});
            skArc(sketch, "E235.filletArc", {"start": v(107.1, 6.85) * mm, "mid": v(107.06, 6.96) * mm, "end": v(106.96, 7) * mm});
            skPoint(sketch, "E236.endSnap0", {"position": v(107.36, 8.14) * mm});
            skLineSegment(sketch, "E237", {"start": v(107.36, 8.14) * mm, "end": v(107.36, -53.3) * mm, "construction": true});
            skLineSegment(sketch, "E238", {"start": v(92.28, 5.27) * mm, "end": v(92.78, 5.27) * mm});
            skLineSegment(sketch, "E239", {"start": v(92.78, 5.27) * mm, "end": v(92.78, 6.85) * mm});
            skLineSegment(sketch, "E240", {"start": v(92.28, 5.27) * mm, "end": v(92.28, 6.85) * mm});
            skArc(sketch, "E241", {"start": v(91.43, 7.32) * mm, "mid": v(92.53, 8.14) * mm, "end": v(93.62, 7.32) * mm});
            skLineSegment(sketch, "E242", {"start": v(91.67, 7) * mm, "end": v(92.13, 7) * mm});
            skLineSegment(sketch, "E243", {"start": v(93.38, 7) * mm, "end": v(92.93, 7) * mm});
            skPoint(sketch, "E244.visualSharp", {"position": v(93.67, 7) * mm});
            skArc(sketch, "E244.filletArc", {"start": v(93.38, 7) * mm, "mid": v(93.58, 7.1) * mm, "end": v(93.62, 7.32) * mm});
            skPoint(sketch, "E245.visualSharp", {"position": v(91.39, 7) * mm});
            skArc(sketch, "E245.filletArc", {"start": v(91.43, 7.32) * mm, "mid": v(91.47, 7.1) * mm, "end": v(91.67, 7) * mm});
            skPoint(sketch, "E246.visualSharp", {"position": v(92.78, 7) * mm});
            skArc(sketch, "E246.filletArc", {"start": v(92.93, 7) * mm, "mid": v(92.82, 6.96) * mm, "end": v(92.78, 6.85) * mm});
            skPoint(sketch, "E247.visualSharp", {"position": v(92.28, 7) * mm});
            skArc(sketch, "E247.filletArc", {"start": v(92.28, 6.85) * mm, "mid": v(92.23, 6.96) * mm, "end": v(92.13, 7) * mm});
            skPoint(sketch, "E248.endSnap0", {"position": v(92.53, 8.14) * mm});
            skLineSegment(sketch, "E249", {"start": v(92.53, 8.14) * mm, "end": v(92.53, -53.3) * mm, "construction": true});
            skLineSegment(sketch, "E250", {"start": v(78.28, 5.27) * mm, "end": v(78.78, 5.27) * mm});
            skLineSegment(sketch, "E251", {"start": v(78.78, 5.27) * mm, "end": v(78.78, 6.85) * mm});
            skLineSegment(sketch, "E252", {"start": v(78.28, 5.27) * mm, "end": v(78.28, 6.85) * mm});
            skArc(sketch, "E253", {"start": v(77.44, 7.32) * mm, "mid": v(78.53, 8.14) * mm, "end": v(79.63, 7.32) * mm});
            skLineSegment(sketch, "E254", {"start": v(77.68, 7) * mm, "end": v(78.13, 7) * mm});
            skLineSegment(sketch, "E255", {"start": v(79.39, 7) * mm, "end": v(78.93, 7) * mm});
            skPoint(sketch, "E256.visualSharp", {"position": v(79.67, 7) * mm});
            skArc(sketch, "E256.filletArc", {"start": v(79.39, 7) * mm, "mid": v(79.59, 7.1) * mm, "end": v(79.63, 7.32) * mm});
            skPoint(sketch, "E257.visualSharp", {"position": v(77.4, 7) * mm});
            skArc(sketch, "E257.filletArc", {"start": v(77.44, 7.32) * mm, "mid": v(77.48, 7.1) * mm, "end": v(77.68, 7) * mm});
            skPoint(sketch, "E258.visualSharp", {"position": v(78.78, 7) * mm});
            skArc(sketch, "E258.filletArc", {"start": v(78.93, 7) * mm, "mid": v(78.83, 6.96) * mm, "end": v(78.78, 6.85) * mm});
            skPoint(sketch, "E259.visualSharp", {"position": v(78.28, 7) * mm});
            skArc(sketch, "E259.filletArc", {"start": v(78.28, 6.85) * mm, "mid": v(78.24, 6.96) * mm, "end": v(78.13, 7) * mm});
            skPoint(sketch, "E260.endSnap0", {"position": v(78.53, 8.14) * mm});
            skLineSegment(sketch, "E261", {"start": v(78.53, 8.14) * mm, "end": v(78.53, -53.3) * mm, "construction": true});
            skLineSegment(sketch, "E262", {"start": v(65.07, 5.27) * mm, "end": v(65.57, 5.27) * mm});
            skLineSegment(sketch, "E263", {"start": v(65.57, 5.27) * mm, "end": v(65.57, 6.85) * mm});
            skLineSegment(sketch, "E264", {"start": v(65.07, 5.27) * mm, "end": v(65.07, 6.85) * mm});
            skArc(sketch, "E265", {"start": v(64.23, 7.32) * mm, "mid": v(65.32, 8.14) * mm, "end": v(66.42, 7.32) * mm});
            skLineSegment(sketch, "E266", {"start": v(64.47, 7) * mm, "end": v(64.92, 7) * mm});
            skLineSegment(sketch, "E267", {"start": v(66.18, 7) * mm, "end": v(65.72, 7) * mm});
            skPoint(sketch, "E268.visualSharp", {"position": v(66.46, 7) * mm});
            skArc(sketch, "E268.filletArc", {"start": v(66.18, 7) * mm, "mid": v(66.38, 7.1) * mm, "end": v(66.42, 7.32) * mm});
            skPoint(sketch, "E269.visualSharp", {"position": v(64.18, 7) * mm});
            skArc(sketch, "E269.filletArc", {"start": v(64.23, 7.32) * mm, "mid": v(64.27, 7.1) * mm, "end": v(64.47, 7) * mm});
            skPoint(sketch, "E270.visualSharp", {"position": v(65.57, 7) * mm});
            skArc(sketch, "E270.filletArc", {"start": v(65.72, 7) * mm, "mid": v(65.62, 6.96) * mm, "end": v(65.57, 6.85) * mm});
            skPoint(sketch, "E271.visualSharp", {"position": v(65.07, 7) * mm});
            skArc(sketch, "E271.filletArc", {"start": v(65.07, 6.85) * mm, "mid": v(65.03, 6.96) * mm, "end": v(64.92, 7) * mm});
            skPoint(sketch, "E272.endSnap0", {"position": v(65.32, 8.14) * mm});
            skLineSegment(sketch, "E273", {"start": v(65.32, 8.14) * mm, "end": v(65.32, -53.3) * mm, "construction": true});
            skLineSegment(sketch, "E274", {"start": v(52.6, 5.27) * mm, "end": v(53.1, 5.27) * mm});
            skLineSegment(sketch, "E275", {"start": v(53.1, 5.27) * mm, "end": v(53.1, 6.85) * mm});
            skLineSegment(sketch, "E276", {"start": v(52.6, 5.27) * mm, "end": v(52.6, 6.85) * mm});
            skArc(sketch, "E277", {"start": v(51.76, 7.32) * mm, "mid": v(52.85, 8.14) * mm, "end": v(53.95, 7.32) * mm});
            skLineSegment(sketch, "E278", {"start": v(52, 7) * mm, "end": v(52.45, 7) * mm});
            skLineSegment(sketch, "E279", {"start": v(53.7, 7) * mm, "end": v(53.25, 7) * mm});
            skPoint(sketch, "E280.visualSharp", {"position": v(54, 7) * mm});
            skArc(sketch, "E280.filletArc", {"start": v(53.7, 7) * mm, "mid": v(53.9, 7.1) * mm, "end": v(53.95, 7.32) * mm});
            skPoint(sketch, "E281.visualSharp", {"position": v(51.71, 7) * mm});
            skArc(sketch, "E281.filletArc", {"start": v(51.76, 7.32) * mm, "mid": v(51.8, 7.1) * mm, "end": v(52, 7) * mm});
            skPoint(sketch, "E282.visualSharp", {"position": v(53.1, 7) * mm});
            skArc(sketch, "E282.filletArc", {"start": v(53.25, 7) * mm, "mid": v(53.15, 6.96) * mm, "end": v(53.1, 6.85) * mm});
            skPoint(sketch, "E283.visualSharp", {"position": v(52.6, 7) * mm});
            skArc(sketch, "E283.filletArc", {"start": v(52.6, 6.85) * mm, "mid": v(52.56, 6.96) * mm, "end": v(52.45, 7) * mm});
            skPoint(sketch, "E284.endSnap0", {"position": v(52.85, 8.14) * mm});
            skLineSegment(sketch, "E285", {"start": v(52.85, 8.14) * mm, "end": v(52.85, -53.3) * mm, "construction": true});
            skLineSegment(sketch, "E286", {"start": v(40.84, 5.27) * mm, "end": v(41.34, 5.27) * mm});
            skLineSegment(sketch, "E287", {"start": v(41.34, 5.27) * mm, "end": v(41.34, 6.85) * mm});
            skLineSegment(sketch, "E288", {"start": v(40.84, 5.27) * mm, "end": v(40.84, 6.85) * mm});
            skArc(sketch, "E289", {"start": v(40, 7.32) * mm, "mid": v(41.09, 8.14) * mm, "end": v(42.18, 7.32) * mm});
            skLineSegment(sketch, "E290", {"start": v(40.23, 7) * mm, "end": v(40.69, 7) * mm});
            skLineSegment(sketch, "E291", {"start": v(41.94, 7) * mm, "end": v(41.49, 7) * mm});
            skPoint(sketch, "E292.visualSharp", {"position": v(42.23, 7) * mm});
            skArc(sketch, "E292.filletArc", {"start": v(41.94, 7) * mm, "mid": v(42.14, 7.1) * mm, "end": v(42.18, 7.32) * mm});
            skPoint(sketch, "E293.visualSharp", {"position": v(39.95, 7) * mm});
            skArc(sketch, "E293.filletArc", {"start": v(40, 7.32) * mm, "mid": v(40.03, 7.1) * mm, "end": v(40.23, 7) * mm});
            skPoint(sketch, "E294.visualSharp", {"position": v(41.34, 7) * mm});
            skArc(sketch, "E294.filletArc", {"start": v(41.49, 7) * mm, "mid": v(41.38, 6.96) * mm, "end": v(41.34, 6.85) * mm});
            skPoint(sketch, "E295.visualSharp", {"position": v(40.84, 7) * mm});
            skArc(sketch, "E295.filletArc", {"start": v(40.84, 6.85) * mm, "mid": v(40.8, 6.96) * mm, "end": v(40.69, 7) * mm});
            skPoint(sketch, "E296.endSnap0", {"position": v(41.09, 8.14) * mm});
            skLineSegment(sketch, "E297", {"start": v(41.09, 8.14) * mm, "end": v(41.09, -53.3) * mm, "construction": true});
            skLineSegment(sketch, "E298", {"start": v(29.73, 5.27) * mm, "end": v(30.23, 5.27) * mm});
            skLineSegment(sketch, "E299", {"start": v(30.23, 5.27) * mm, "end": v(30.23, 6.85) * mm});
            skLineSegment(sketch, "E300", {"start": v(29.73, 5.27) * mm, "end": v(29.73, 6.85) * mm});
            skArc(sketch, "E301", {"start": v(28.88, 7.32) * mm, "mid": v(29.98, 8.14) * mm, "end": v(31.07, 7.32) * mm});
            skLineSegment(sketch, "E302", {"start": v(29.12, 7) * mm, "end": v(29.58, 7) * mm});
            skLineSegment(sketch, "E303", {"start": v(30.83, 7) * mm, "end": v(30.38, 7) * mm});
            skPoint(sketch, "E304.visualSharp", {"position": v(31.12, 7) * mm});
            skArc(sketch, "E304.filletArc", {"start": v(30.83, 7) * mm, "mid": v(31.03, 7.1) * mm, "end": v(31.07, 7.32) * mm});
            skPoint(sketch, "E305.visualSharp", {"position": v(28.84, 7) * mm});
            skArc(sketch, "E305.filletArc", {"start": v(28.88, 7.32) * mm, "mid": v(28.92, 7.1) * mm, "end": v(29.12, 7) * mm});
            skPoint(sketch, "E306.visualSharp", {"position": v(30.23, 7) * mm});
            skArc(sketch, "E306.filletArc", {"start": v(30.38, 7) * mm, "mid": v(30.27, 6.96) * mm, "end": v(30.23, 6.85) * mm});
            skPoint(sketch, "E307.visualSharp", {"position": v(29.73, 7) * mm});
            skArc(sketch, "E307.filletArc", {"start": v(29.73, 6.85) * mm, "mid": v(29.68, 6.96) * mm, "end": v(29.58, 7) * mm});
            skPoint(sketch, "E308.endSnap0", {"position": v(29.98, 8.14) * mm});
            skLineSegment(sketch, "E309", {"start": v(29.98, 8.14) * mm, "end": v(29.98, -53.3) * mm, "construction": true});
            skLineSegment(sketch, "E310", {"start": v(19.24, 5.27) * mm, "end": v(19.74, 5.27) * mm});
            skLineSegment(sketch, "E311", {"start": v(19.74, 5.27) * mm, "end": v(19.74, 6.85) * mm});
            skLineSegment(sketch, "E312", {"start": v(19.24, 5.27) * mm, "end": v(19.24, 6.85) * mm});
            skArc(sketch, "E313", {"start": v(18.4, 7.32) * mm, "mid": v(19.5, 8.14) * mm, "end": v(20.59, 7.32) * mm});
            skLineSegment(sketch, "E314", {"start": v(18.64, 7) * mm, "end": v(19.1, 7) * mm});
            skLineSegment(sketch, "E315", {"start": v(20.35, 7) * mm, "end": v(19.9, 7) * mm});
            skPoint(sketch, "E316.visualSharp", {"position": v(20.63, 7) * mm});
            skArc(sketch, "E316.filletArc", {"start": v(20.35, 7) * mm, "mid": v(20.55, 7.1) * mm, "end": v(20.59, 7.32) * mm});
            skPoint(sketch, "E317.visualSharp", {"position": v(18.35, 7) * mm});
            skArc(sketch, "E317.filletArc", {"start": v(18.4, 7.32) * mm, "mid": v(18.44, 7.1) * mm, "end": v(18.64, 7) * mm});
            skPoint(sketch, "E318.visualSharp", {"position": v(19.74, 7) * mm});
            skArc(sketch, "E318.filletArc", {"start": v(19.9, 7) * mm, "mid": v(19.79, 6.96) * mm, "end": v(19.74, 6.85) * mm});
            skPoint(sketch, "E319.visualSharp", {"position": v(19.24, 7) * mm});
            skArc(sketch, "E319.filletArc", {"start": v(19.24, 6.85) * mm, "mid": v(19.2, 6.96) * mm, "end": v(19.1, 7) * mm});
            skPoint(sketch, "E320.endSnap0", {"position": v(19.5, 8.14) * mm});
            skLineSegment(sketch, "E321", {"start": v(19.5, 8.14) * mm, "end": v(19.5, -53.3) * mm, "construction": true});
            skLineSegment(sketch, "E322", {"start": v(9.35, 5.27) * mm, "end": v(9.85, 5.27) * mm});
            skLineSegment(sketch, "E323", {"start": v(9.85, 5.27) * mm, "end": v(9.85, 6.85) * mm});
            skLineSegment(sketch, "E324", {"start": v(9.35, 5.27) * mm, "end": v(9.35, 6.85) * mm});
            skArc(sketch, "E325", {"start": v(8.5, 7.32) * mm, "mid": v(9.6, 8.14) * mm, "end": v(10.7, 7.32) * mm});
            skLineSegment(sketch, "E326", {"start": v(8.74, 7) * mm, "end": v(9.2, 7) * mm});
            skLineSegment(sketch, "E327", {"start": v(10.45, 7) * mm, "end": v(10, 7) * mm});
            skPoint(sketch, "E328.visualSharp", {"position": v(10.74, 7) * mm});
            skArc(sketch, "E328.filletArc", {"start": v(10.45, 7) * mm, "mid": v(10.65, 7.1) * mm, "end": v(10.7, 7.32) * mm});
            skPoint(sketch, "E329.visualSharp", {"position": v(8.46, 7) * mm});
            skArc(sketch, "E329.filletArc", {"start": v(8.5, 7.32) * mm, "mid": v(8.54, 7.1) * mm, "end": v(8.74, 7) * mm});
            skPoint(sketch, "E330.visualSharp", {"position": v(9.85, 7) * mm});
            skArc(sketch, "E330.filletArc", {"start": v(10, 7) * mm, "mid": v(9.89, 6.96) * mm, "end": v(9.85, 6.85) * mm});
            skPoint(sketch, "E331.visualSharp", {"position": v(9.35, 7) * mm});
            skArc(sketch, "E331.filletArc", {"start": v(9.35, 6.85) * mm, "mid": v(9.3, 6.96) * mm, "end": v(9.2, 7) * mm});
            skPoint(sketch, "E332.endSnap0", {"position": v(9.6, 8.14) * mm});
            skLineSegment(sketch, "E333", {"start": v(9.6, 8.14) * mm, "end": v(9.6, -53.3) * mm, "construction": true});
            skLineSegment(sketch, "E334", {"start": v(0, 5.27) * mm, "end": v(0.5, 5.27) * mm});
            skLineSegment(sketch, "E335", {"start": v(0.5, 5.27) * mm, "end": v(0.5, 6.85) * mm});
            skLineSegment(sketch, "E336", {"start": v(0, 5.27) * mm, "end": v(0, 6.85) * mm});
            skArc(sketch, "E337", {"start": v(-0.84, 7.32) * mm, "mid": v(0.25, 8.14) * mm, "end": v(1.34, 7.32) * mm});
            skLineSegment(sketch, "E338", {"start": v(-0.6, 7) * mm, "end": v(-0.15, 7) * mm});
            skLineSegment(sketch, "E339", {"start": v(1.1, 7) * mm, "end": v(0.65, 7) * mm});
            skPoint(sketch, "E340.visualSharp", {"position": v(1.39, 7) * mm});
            skArc(sketch, "E340.filletArc", {"start": v(1.1, 7) * mm, "mid": v(1.3, 7.1) * mm, "end": v(1.34, 7.32) * mm});
            skPoint(sketch, "E341.visualSharp", {"position": v(-0.9, 7) * mm});
            skArc(sketch, "E341.filletArc", {"start": v(-0.84, 7.32) * mm, "mid": v(-0.8, 7.1) * mm, "end": v(-0.6, 7) * mm});
            skPoint(sketch, "E342.visualSharp", {"position": v(0.5, 7) * mm});
            skArc(sketch, "E342.filletArc", {"start": v(0.65, 7) * mm, "mid": v(0.54, 6.96) * mm, "end": v(0.5, 6.85) * mm});
            skPoint(sketch, "E343.visualSharp", {"position": v(0, 7) * mm});
            skArc(sketch, "E343.filletArc", {"start": v(0, 6.85) * mm, "mid": v(-0.04, 6.96) * mm, "end": v(-0.15, 7) * mm});
            skPoint(sketch, "E344.endSnap0", {"position": v(0.25, 8.14) * mm});
            skLineSegment(sketch, "E345", {"start": v(0.25, 8.14) * mm, "end": v(0.25, -53.3) * mm, "construction": true});
            skLineSegment(sketch, "E346", {"start": v(0.25, -53.3) * mm, "end": v(436.24, -53.3) * mm, "construction": true});
            skSolve(sketch);
        }
        {
            var Q0;
            Q0 = qSketchRegion(id + "F1", true);
            var Q1;
            Q1=sQuery(id+"F1.wireOp",EDGE,"E346");
            revolve(context, id + "F2", {"surfaceOperationType" : NewSurfaceOperationType.NEW, "entities" : qUnion([Q0]), "axis" : qUnion([Q1]), "revolveType" : RevolveType.SYMMETRIC, "angle" : 60 * degree});
        }
        {
            var Q0;
            Q0=qCreatedBy(makeId("Top.planeOp"),FACE);
            var sketch = newSketch(context, id + "F3", { "sketchPlane" : qUnion([Q0])});
            skLineSegment(sketch, "E347.bottom", {"start": v(2.76, 28) * mm, "end": v(78.76, 28) * mm});
            skLineSegment(sketch, "E348", {"start": v(78.76, 28) * mm, "end": v(471.76, 21.5) * mm});
            skLineSegment(sketch, "E349", {"start": v(471.76, 21.5) * mm, "end": v(471.76, -21.5) * mm});
            skLineSegment(sketch, "E350", {"start": v(471.76, -21.5) * mm, "end": v(78.76, -28) * mm});
            skLineSegment(sketch, "E351", {"start": v(-6.24, 37.5) * mm, "end": v(493.76, 37.5) * mm});
            skLineSegment(sketch, "E352", {"start": v(493.76, 37.5) * mm, "end": v(493.76, -37.5) * mm});
            skLineSegment(sketch, "E353", {"start": v(493.76, -37.5) * mm, "end": v(-6.24, -37.5) * mm});
            skLineSegment(sketch, "E354", {"start": v(-6.24, 12.5) * mm, "end": v(-1.24, 12.5) * mm});
            skLineSegment(sketch, "E355", {"start": v(-1.24, 12.5) * mm, "end": v(-1.24, 24) * mm});
            skArc(sketch, "E356.filletArc", {"start": v(2.76, 28) * mm, "mid": v(-0.07, 26.83) * mm, "end": v(-1.24, 24) * mm});
            skLineSegment(sketch, "E357", {"start": v(-1.24, -24) * mm, "end": v(-1.24, -12.5) * mm});
            skLineSegment(sketch, "E358", {"start": v(-1.24, -12.5) * mm, "end": v(-6.24, -12.5) * mm});
            skLineSegment(sketch, "E359", {"start": v(78.76, -28) * mm, "end": v(2.76, -28) * mm});
            skPoint(sketch, "E360.visualSharp", {"position": v(-1.24, -28) * mm});
            skArc(sketch, "E360.filletArc", {"start": v(-1.24, -24) * mm, "mid": v(-0.07, -26.83) * mm, "end": v(2.76, -28) * mm});
            skLineSegment(sketch, "E361", {"start": v(471.76, 0) * mm, "end": v(-6.24, 0) * mm, "construction": true});
            skLineSegment(sketch, "E362", {"start": v(-6.24, 37.5) * mm, "end": v(-6.24, 12.5) * mm});
            skLineSegment(sketch, "E363", {"start": v(-6.24, -12.5) * mm, "end": v(-6.24, -37.5) * mm});
            skLineSegment(sketch, "E364", {"start": v(-6.24, 12.5) * mm, "end": v(-6.24, -12.5) * mm, "construction": true});
            skSolve(sketch);
        }
        {
            var Q0;
            Q0 = qSketchRegion(id + "F3", true);
            extrude(context, id + "F4", {"entities" : qUnion([Q0]), "operationType" : NewBodyOperationType.REMOVE, "endBound" : BoundingType.SYMMETRIC, "oppositeDirection" : true, "depth" : 25 * mm, "offsetDistance" : 25 * mm});
        }
    });
